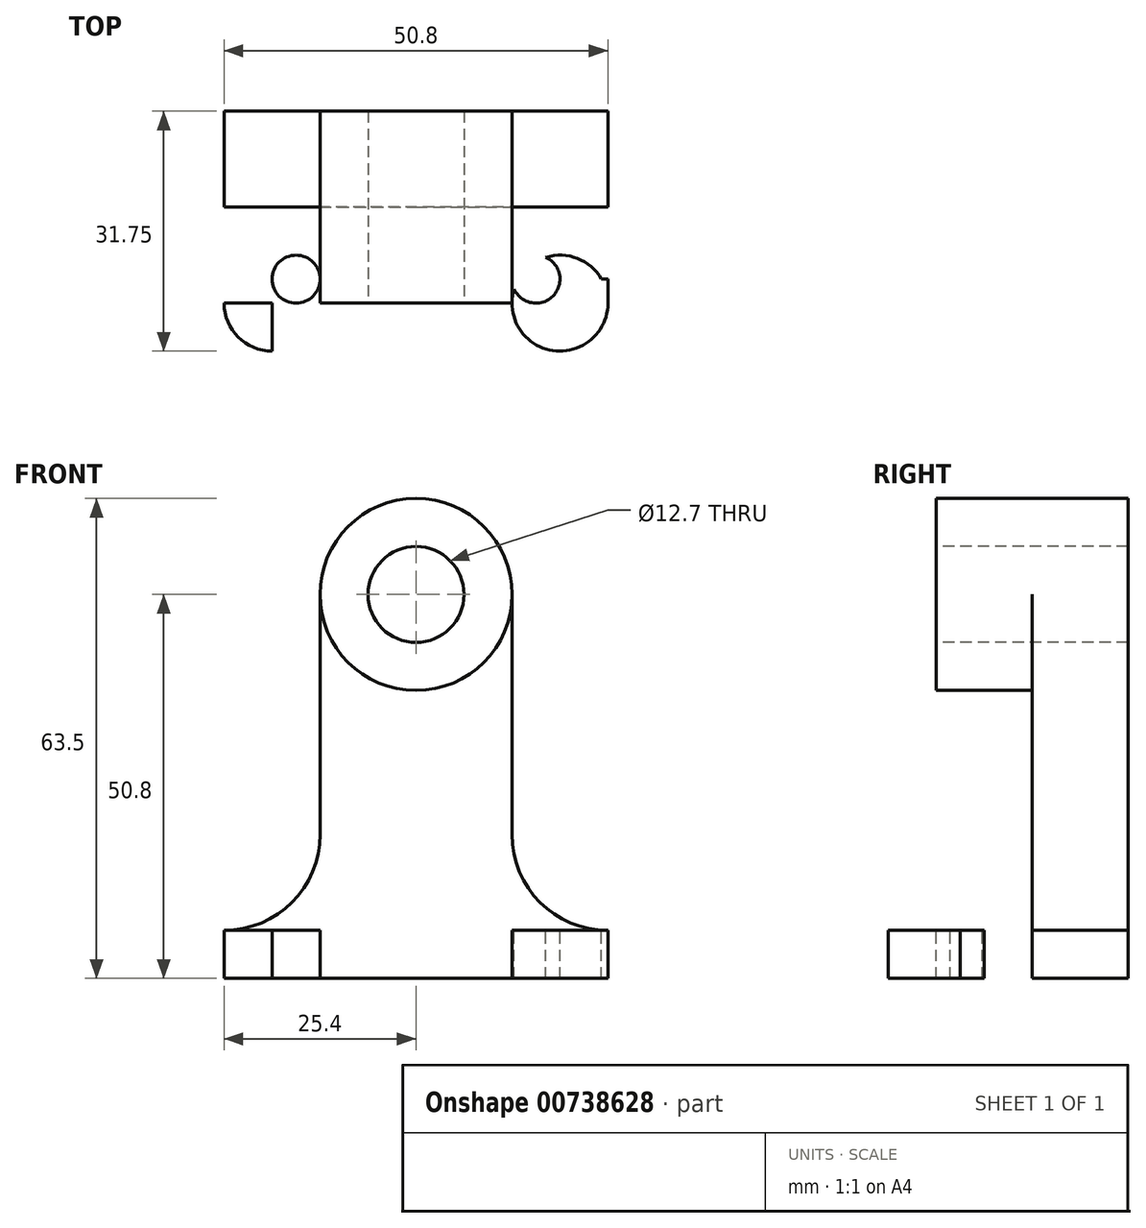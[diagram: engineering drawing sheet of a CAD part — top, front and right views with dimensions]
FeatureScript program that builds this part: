
annotation { "Feature Type Name" : "Feature", "Feature Type Description" : "" }
export const myFeature = defineFeature(function(context is Context, id is Id, definition is map)
    precondition{}
    {
        {
            var Q0;
            Q0=qCreatedBy(makeId("Front.planeOp"),FACE);
            var sketch = newSketch(context, id + "F0", { "sketchPlane" : qUnion([Q0])});
            skLineSegment(sketch, "E0.bottom", {"start": v(0, 0) * mm, "end": v(50.8, 0) * mm});
            skLineSegment(sketch, "E0.top", {"start": v(0, 6.35) * mm, "end": v(50.8, 6.35) * mm});
            skLineSegment(sketch, "E0.left", {"start": v(0, 0) * mm, "end": v(0, 6.35) * mm});
            skLineSegment(sketch, "E0.right", {"start": v(50.8, 0) * mm, "end": v(50.8, 6.35) * mm});
            skLineSegment(sketch, "E1", {"start": v(50.8, 6.35) * mm, "end": v(50.8, 19.05) * mm});
            skLineSegment(sketch, "E2", {"start": v(50.8, 19.05) * mm, "end": v(38.1, 19.05) * mm});
            skCircle(sketch, "E3", {"center": v(50.8, 19.05) * mm, "radius": 12.7 * mm});
            skLineSegment(sketch, "E4", {"start": v(0, 6.35) * mm, "end": v(0, 19.05) * mm});
            skLineSegment(sketch, "E5", {"start": v(0, 19.05) * mm, "end": v(12.7, 19.05) * mm});
            skCircle(sketch, "E6", {"center": v(0, 19.05) * mm, "radius": 12.7 * mm});
            skLineSegment(sketch, "E7", {"start": v(12.7, 19.05) * mm, "end": v(12.7, 50.8) * mm});
            skLineSegment(sketch, "E8", {"start": v(38.1, 19.05) * mm, "end": v(38.1, 50.8) * mm});
            skLineSegment(sketch, "E9", {"start": v(12.7, 50.8) * mm, "end": v(38.1, 50.8) * mm});
            skCircle(sketch, "E10", {"center": v(25.4, 50.8) * mm, "radius": 12.7 * mm});
            skCircle(sketch, "E11", {"center": v(25.4, 50.8) * mm, "radius": 6.35 * mm});
            skSolve(sketch);
        }
        {
            var Q0;
            Q0=makeQuery(id+"F0.imprint","IMPRINT",FACE,{"disambiguationData":[TD([[makeQuery(id+"F0.imprint","IMPRINT",EDGE,{"derivedFrom":sQuery(id+"F0.wireOp",EDGE,"E0.bottom")}),1.0]])]});
            var Q1;
            {var subQ1=sQuery(id+"F0.wireOp",EDGE,"E0.top");Q1=makeQuery(id+"F0.imprint","IMPRINT",FACE,{"disambiguationData":[TD([[makeQuery(id+"F0.imprint","IMPRINT",EDGE,{"derivedFrom":subQ1}),1.0]])]});}
            var Q2;
            {var subQ1=sQuery(id+"F0.wireOp",EDGE,"E9");var subQ3=sQuery(id+"F0.wireOp",EDGE,"E11");var subQ4=makeQuery(id+"F0.imprint","INTERSECT",VERTEX,{"disambiguationData":[OD(0.0)],"derivedFrom":[subQ1,subQ3]});Q2=makeQuery(id+"F0.imprint","IMPRINT",FACE,{"disambiguationData":[TD([[makeQuery(id+"F0.imprint","IMPRINT",EDGE,{"disambiguationData":[TD([[subQ4,-1.0]])],"derivedFrom":subQ3}),-1.0]])]});}
            var Q3;
            {var subQ1=sQuery(id+"F0.wireOp",EDGE,"E9");var subQ3=sQuery(id+"F0.wireOp",EDGE,"E11");var subQ4=makeQuery(id+"F0.imprint","INTERSECT",VERTEX,{"disambiguationData":[OD(0.0)],"derivedFrom":[subQ1,subQ3]});Q3=makeQuery(id+"F0.imprint","IMPRINT",FACE,{"disambiguationData":[TD([[makeQuery(id+"F0.imprint","IMPRINT",EDGE,{"disambiguationData":[TD([[subQ4,1.0]])],"derivedFrom":subQ3}),-1.0]])]});}
            extrude(context, id + "F1", {"entities" : qUnion([Q0, Q1, Q2, Q3]), "oppositeDirection" : true, "depth" : 31.75 * mm, "offsetDistance" : 25.4 * mm});
        }
        {
            var Q0;
            Q0=makeQuery(id+"F1.opExtrude","CAP_FACE",FACE,{"disambiguationData":[OSD([sQuery(id+"F0.wireOp",EDGE,"E0.bottom"),sQuery(id+"F0.wireOp",EDGE,"E0.left"),sQuery(id+"F0.wireOp",EDGE,"E0.right"),sQuery(id+"F0.wireOp",EDGE,"E3"),sQuery(id+"F0.wireOp",EDGE,"E6"),sQuery(id+"F0.wireOp",EDGE,"E7"),sQuery(id+"F0.wireOp",EDGE,"E8"),sQuery(id+"F0.wireOp",EDGE,"E10"),sQuery(id+"F0.wireOp",EDGE,"E11")])],"isStart":true});
            var sketch = newSketch(context, id + "F2", { "sketchPlane" : qUnion([Q0])});
            skLineSegment(sketch, "E12", {"start": v(0, 6.35) * mm, "end": v(50.8, 6.35) * mm});
            skLineSegment(sketch, "E13", {"start": v(38.1, 50.8) * mm, "end": v(12.7, 50.8) * mm});
            skCircle(sketch, "E14", {"center": v(25.4, 50.8) * mm, "radius": 12.7 * mm});
            skSolve(sketch);
        }
        {
            var Q0;
            Q0=makeQuery(id+"F2.imprint","IMPRINT",FACE,{"disambiguationData":[TD([[makeQuery(id+"F2.imprint","IMPRINT",EDGE,{"derivedFrom":sQuery(id+"F2.wireOp",EDGE,"E12")}),1.0]])]});
            extrude(context, id + "F3", {"entities" : qUnion([Q0]), "operationType" : NewBodyOperationType.REMOVE, "oppositeDirection" : true, "depth" : 19.05 * mm, "offsetDistance" : 25.4 * mm});
        }
        {
            var Q0;
            {var subQ0=sQuery(id+"F0.wireOp",EDGE,"E10");var subQ1=sQuery(id+"F0.wireOp",EDGE,"E11");Q0=makeQuery(id+"F3.boolean.opBoolean","SPLIT",FACE,{"disambiguationData":[TD([makeQuery(id+"F1.opExtrude","SWEPT_FACE",FACE,{"disambiguationData":[OSD([subQ0])]})])],"derivedFrom":makeQuery(id+"F1.opExtrude","CAP_FACE",FACE,{"disambiguationData":[OSD([sQuery(id+"F0.wireOp",EDGE,"E0.bottom"),sQuery(id+"F0.wireOp",EDGE,"E0.left"),sQuery(id+"F0.wireOp",EDGE,"E0.right"),sQuery(id+"F0.wireOp",EDGE,"E3"),sQuery(id+"F0.wireOp",EDGE,"E6"),sQuery(id+"F0.wireOp",EDGE,"E7"),sQuery(id+"F0.wireOp",EDGE,"E8"),subQ0,subQ1])],"isStart":true})});}
            extrude(context, id + "F4", {"entities" : qUnion([Q0]), "operationType" : NewBodyOperationType.REMOVE, "oppositeDirection" : true, "depth" : 6.35 * mm, "offsetDistance" : 25.4 * mm});
        }
        {
            var Q0;
            Q0=makeQuery(id+"F3.boolean.opBoolean","COPY",FACE,{"derivedFrom":makeQuery(id+"F3.opExtrude","SWEPT_FACE",FACE,{"disambiguationData":[OSD([sQuery(id+"F2.wireOp",EDGE,"E12")])]})});
            var sketch = newSketch(context, id + "F5", { "sketchPlane" : qUnion([Q0])});
            skLineSegment(sketch, "E15", {"start": v(50.8, 0) * mm, "end": v(50.8, 6.35) * mm});
            skLineSegment(sketch, "E16", {"start": v(50.8, 6.35) * mm, "end": v(44.45, 6.35) * mm});
            skCircle(sketch, "E17", {"center": v(44.45, 6.35) * mm, "radius": 6.35 * mm});
            skLineSegment(sketch, "E18.bottom", {"start": v(0, 0) * mm, "end": v(6.35, 0) * mm});
            skLineSegment(sketch, "E18.top", {"start": v(0, 6.35) * mm, "end": v(6.35, 6.35) * mm});
            skLineSegment(sketch, "E18.left", {"start": v(0, 0) * mm, "end": v(0, 6.35) * mm});
            skLineSegment(sketch, "E18.right", {"start": v(6.35, 0) * mm, "end": v(6.35, 6.35) * mm});
            skCircle(sketch, "E19", {"center": v(6.35, 6.35) * mm, "radius": 6.35 * mm});
            skLineSegment(sketch, "E20", {"start": v(0, 0) * mm, "end": v(0, 19.05) * mm});
            skLineSegment(sketch, "E21", {"start": v(0, 9.53) * mm, "end": v(19.05, 9.53) * mm});
            skCircle(sketch, "E22", {"center": v(9.53, 9.53) * mm, "radius": 3.18 * mm});
            skLineSegment(sketch, "E23", {"start": v(50.8, 0) * mm, "end": v(50.8, 19.05) * mm});
            skLineSegment(sketch, "E24", {"start": v(50.8, 9.53) * mm, "end": v(31.75, 9.53) * mm});
            skCircle(sketch, "E25", {"center": v(41.28, 9.53) * mm, "radius": 3.18 * mm});
            skSolve(sketch);
        }
        {
            var Q0;
            {var subQ0=sQuery(id+"F5.wireOp",EDGE,"E21");var subQ1=sQuery(id+"F5.wireOp",EDGE,"E19");var subQ2=makeQuery(id+"F5.imprint","INTERSECT",VERTEX,{"disambiguationData":[OD(0.0)],"derivedFrom":[subQ1,subQ0]});Q0=makeQuery(id+"F5.imprint","IMPRINT",FACE,{"disambiguationData":[TD([[makeQuery(id+"F5.imprint","IMPRINT",EDGE,{"disambiguationData":[TD([[subQ2,-1.0]])],"derivedFrom":subQ1}),-1.0]])]});}
            var Q1;
            {var subQ0=sQuery(id+"F5.wireOp",EDGE,"E21");var subQ1=sQuery(id+"F5.wireOp",EDGE,"E19");var subQ2=makeQuery(id+"F5.imprint","INTERSECT",VERTEX,{"disambiguationData":[OD(0.0)],"derivedFrom":[subQ1,subQ0]});Q1=makeQuery(id+"F5.imprint","IMPRINT",FACE,{"disambiguationData":[TD([[makeQuery(id+"F5.imprint","IMPRINT",EDGE,{"disambiguationData":[TD([[subQ2,-1.0]])],"derivedFrom":subQ1}),1.0]])]});}
            var Q2;
            {var subQ0=sQuery(id+"F5.wireOp",EDGE,"E21");var subQ1=sQuery(id+"F5.wireOp",EDGE,"E19");var subQ2=makeQuery(id+"F5.imprint","INTERSECT",VERTEX,{"disambiguationData":[OD(0.0)],"derivedFrom":[subQ1,subQ0]});Q2=makeQuery(id+"F5.imprint","IMPRINT",FACE,{"disambiguationData":[TD([[makeQuery(id+"F5.imprint","IMPRINT",EDGE,{"disambiguationData":[TD([[subQ2,1.0]])],"derivedFrom":subQ1}),1.0]])]});}
            var Q3;
            {var subQ0=sQuery(id+"F5.wireOp",EDGE,"E21");var subQ1=sQuery(id+"F5.wireOp",EDGE,"E19");var subQ2=makeQuery(id+"F5.imprint","INTERSECT",VERTEX,{"disambiguationData":[OD(0.0)],"derivedFrom":[subQ1,subQ0]});Q3=makeQuery(id+"F5.imprint","IMPRINT",FACE,{"disambiguationData":[TD([[makeQuery(id+"F5.imprint","IMPRINT",EDGE,{"disambiguationData":[TD([[subQ2,1.0]])],"derivedFrom":subQ1}),-1.0]])]});}
            var Q4;
            {var subQ0=sQuery(id+"F5.wireOp",EDGE,"E25");var subQ1=sQuery(id+"F5.wireOp",EDGE,"E17");var subQ2=makeQuery(id+"F5.imprint","INTERSECT",VERTEX,{"disambiguationData":[OD(0.0)],"derivedFrom":[subQ1,subQ0]});Q4=makeQuery(id+"F5.imprint","IMPRINT",FACE,{"disambiguationData":[TD([[makeQuery(id+"F5.imprint","IMPRINT",EDGE,{"disambiguationData":[TD([[subQ2,-1.0]])],"derivedFrom":subQ1}),-1.0]])]});}
            var Q5;
            {var subQ0=sQuery(id+"F5.wireOp",EDGE,"E25");var subQ1=sQuery(id+"F5.wireOp",EDGE,"E17");var subQ2=makeQuery(id+"F5.imprint","INTERSECT",VERTEX,{"disambiguationData":[OD(0.0)],"derivedFrom":[subQ1,subQ0]});Q5=makeQuery(id+"F5.imprint","IMPRINT",FACE,{"disambiguationData":[TD([[makeQuery(id+"F5.imprint","IMPRINT",EDGE,{"disambiguationData":[TD([[subQ2,-1.0]])],"derivedFrom":subQ1}),1.0]])]});}
            var Q6;
            {var subQ0=sQuery(id+"F5.wireOp",EDGE,"E24");var subQ1=sQuery(id+"F5.wireOp",EDGE,"E17");var subQ2=makeQuery(id+"F5.imprint","INTERSECT",VERTEX,{"disambiguationData":[OD(1.0)],"derivedFrom":[subQ1,subQ0]});Q6=makeQuery(id+"F5.imprint","IMPRINT",FACE,{"disambiguationData":[TD([[makeQuery(id+"F5.imprint","IMPRINT",EDGE,{"disambiguationData":[TD([[subQ2,-1.0]])],"derivedFrom":subQ1}),1.0]])]});}
            var Q7;
            {var subQ0=sQuery(id+"F5.wireOp",EDGE,"E24");var subQ1=sQuery(id+"F5.wireOp",EDGE,"E17");var subQ2=makeQuery(id+"F5.imprint","INTERSECT",VERTEX,{"disambiguationData":[OD(1.0)],"derivedFrom":[subQ1,subQ0]});Q7=makeQuery(id+"F5.imprint","IMPRINT",FACE,{"disambiguationData":[TD([[makeQuery(id+"F5.imprint","IMPRINT",EDGE,{"disambiguationData":[TD([[subQ2,-1.0]])],"derivedFrom":subQ1}),-1.0]])]});}
            var Q8;
            {var subQ0=sQuery(id+"F5.wireOp",EDGE,"E23");var subQ1=sQuery(id+"F5.wireOp",EDGE,"E17");var subQ2=makeQuery(id+"F5.imprint","INTERSECT",VERTEX,{"derivedFrom":[subQ1,subQ0]});Q8=makeQuery(id+"F5.imprint","IMPRINT",FACE,{"disambiguationData":[TD([[makeQuery(id+"F5.imprint","IMPRINT",EDGE,{"disambiguationData":[TD([[subQ2,1.0]])],"derivedFrom":subQ1}),-1.0]])]});}
            var Q9;
            {var subQ0=sQuery(id+"F5.wireOp",EDGE,"E18.bottom");Q9=makeQuery(id+"F5.imprint","IMPRINT",FACE,{"disambiguationData":[TD([[makeQuery(id+"F5.imprint","IMPRINT",EDGE,{"derivedFrom":subQ0}),1.0]])]});}
            extrude(context, id + "F6", {"entities" : qUnion([Q0, Q1, Q2, Q3, Q4, Q5, Q6, Q7, Q8, Q9]), "operationType" : NewBodyOperationType.REMOVE, "endBound" : BoundingType.THROUGH_ALL, "oppositeDirection" : true, "depth" : 25.4 * mm, "offsetDistance" : 25.4 * mm});
        }
    });
